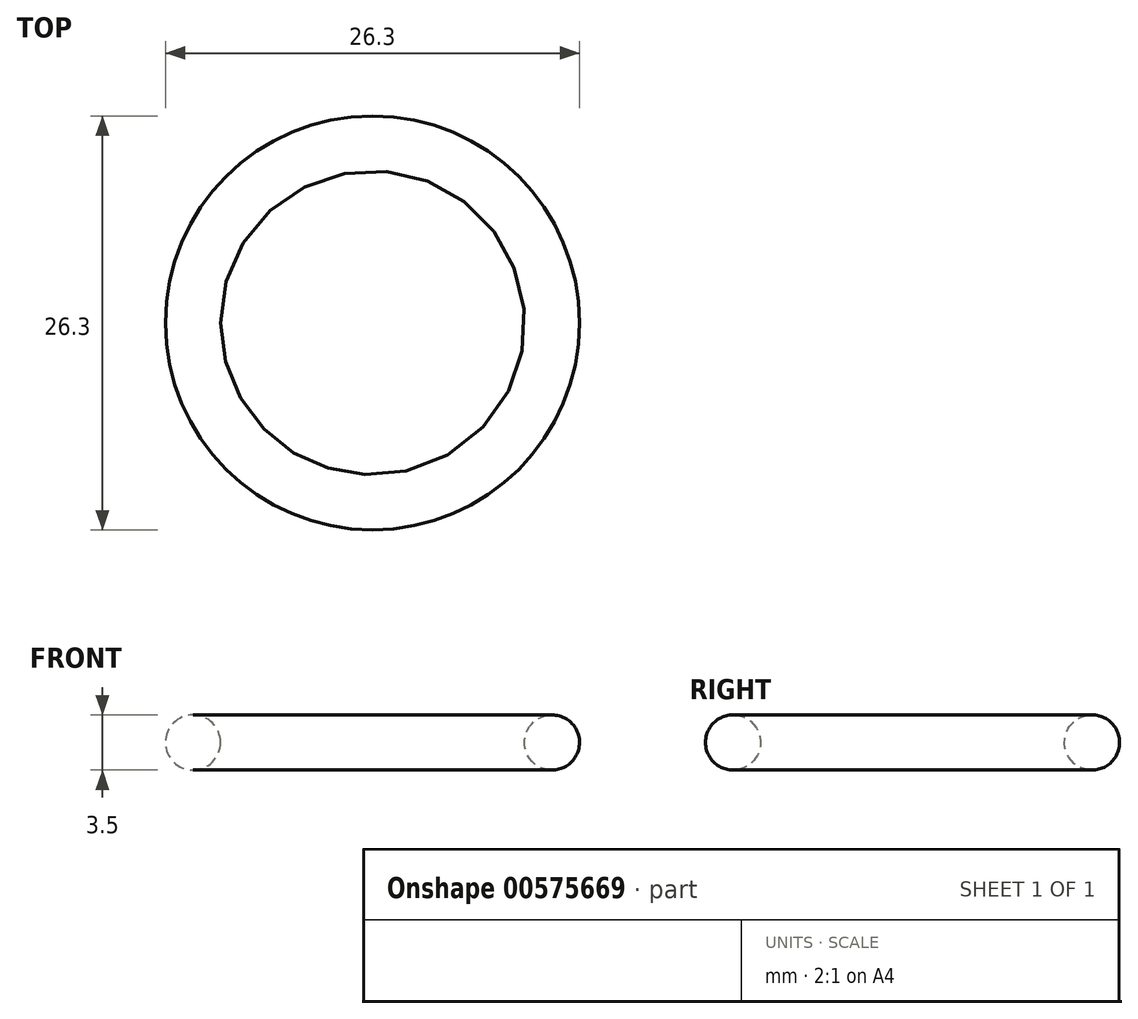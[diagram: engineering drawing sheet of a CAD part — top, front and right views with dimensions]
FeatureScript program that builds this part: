
annotation { "Feature Type Name" : "Feature", "Feature Type Description" : "" }
export const myFeature = defineFeature(function(context is Context, id is Id, definition is map)
    precondition{}
    {
        {
            var Q0;
            Q0=qCreatedBy(makeId("Front.planeOp"),FACE);
            var sketch = newSketch(context, id + "F0", { "sketchPlane" : qUnion([Q0])});
            skLineSegment(sketch, "E0", {"start": v(0, 0) * mm, "end": v(0, 6.44) * mm});
            skCircle(sketch, "E1", {"center": v(-11.4, 0) * mm, "radius": 1.75 * mm});
            skSolve(sketch);
        }
        {
            var Q0;
            Q0=makeQuery(id+"F0.imprint","IMPRINT",FACE,{"disambiguationData":[TD([[makeQuery(id+"F0.imprint","IMPRINT",EDGE,{"derivedFrom":sQuery(id+"F0.wireOp",EDGE,"E1")}),1.0]])]});
            var Q1;
            Q1=sQuery(id+"F0.wireOp",EDGE,"E0");
            revolve(context, id + "F1", {"entities" : qUnion([Q0]), "axis" : qUnion([Q1]), "revolveType" : RevolveType.FULL});
        }
    });
